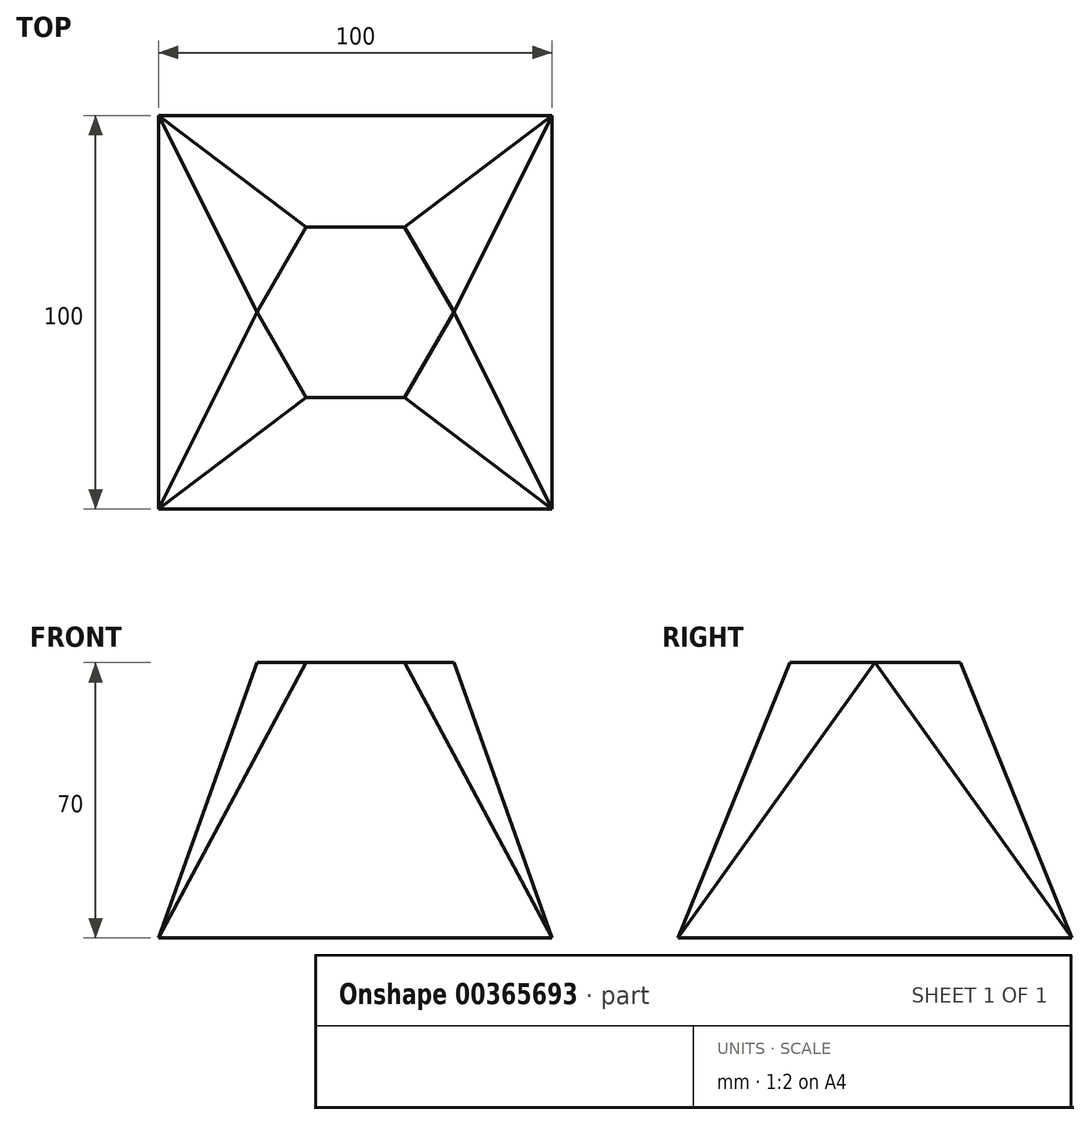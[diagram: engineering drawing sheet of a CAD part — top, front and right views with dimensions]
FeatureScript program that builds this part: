
annotation { "Feature Type Name" : "Feature", "Feature Type Description" : "" }
export const myFeature = defineFeature(function(context is Context, id is Id, definition is map)
    precondition{}
    {
        {
            var Q0;
            Q0=qCreatedBy(makeId("Top.planeOp"),FACE);
            cPlane(context, id + "F0", {"entities" : qUnion([Q0]), "cplaneType" : CPlaneType.OFFSET, "offset" : 70 * mm, "width" : 150 * mm, "height" : 150 * mm});
        }
        {
            var Q0;
            Q0=qCreatedBy(id+"F0.planeOp",FACE);
            var sketch = newSketch(context, id + "F1", { "sketchPlane" : qUnion([Q0])});
            skCircle(sketch, "E0.cCircle", {"center": v(0, 0) * mm, "radius": 25 * mm, "construction": true});
            skLineSegment(sketch, "E0.0", {"start": v(25, 0) * mm, "end": v(12.5, -21.65) * mm});
            skLineSegment(sketch, "E0.1", {"start": v(12.5, -21.65) * mm, "end": v(-12.5, -21.65) * mm});
            skLineSegment(sketch, "E0.2", {"start": v(-12.5, -21.65) * mm, "end": v(-25, 0) * mm});
            skLineSegment(sketch, "E0.3", {"start": v(-25, 0) * mm, "end": v(-12.5, 21.65) * mm});
            skLineSegment(sketch, "E0.4", {"start": v(-12.5, 21.65) * mm, "end": v(12.5, 21.65) * mm});
            skLineSegment(sketch, "E0.5", {"start": v(12.5, 21.65) * mm, "end": v(25, 0) * mm});
            skLineSegment(sketch, "E1", {"start": v(-12.5, 21.65) * mm, "end": v(-12.5, -21.65) * mm});
            skLineSegment(sketch, "E2", {"start": v(12.5, 21.65) * mm, "end": v(12.5, -21.65) * mm});
            skSolve(sketch);
        }
        {
            var Q0;
            Q0=qCreatedBy(makeId("Top.planeOp"),FACE);
            var sketch = newSketch(context, id + "F2", { "sketchPlane" : qUnion([Q0])});
            skLineSegment(sketch, "E3.bottom", {"start": v(50, -50) * mm, "end": v(-50, -50) * mm});
            skLineSegment(sketch, "E3.top", {"start": v(50, 50) * mm, "end": v(-50, 50) * mm});
            skLineSegment(sketch, "E3.left", {"start": v(50, -50) * mm, "end": v(50, 50) * mm});
            skLineSegment(sketch, "E3.right", {"start": v(-50, -50) * mm, "end": v(-50, 50) * mm});
            skPoint(sketch, "E3.middle", {"position": v(0, 0) * mm});
            skSolve(sketch);
        }
        {
            var Q0;
            Q0=makeQuery(id+"F1.imprint","IMPRINT",FACE,{"disambiguationData":[TD([[makeQuery(id+"F1.imprint","IMPRINT",EDGE,{"derivedFrom":sQuery(id+"F1.wireOp",EDGE,"E0.1")}),-1.0]])]});
            var Q1;
            Q1=makeQuery(id+"F2.imprint","IMPRINT",FACE,{"disambiguationData":[TD([[makeQuery(id+"F2.imprint","IMPRINT",EDGE,{"derivedFrom":sQuery(id+"F2.wireOp",EDGE,"E3.bottom")}),-1.0]])]});
            loft(context, id + "F3", {"sheetProfilesArray" : [{ "sheetProfileEntities" : qUnion([Q0]) }, { "sheetProfileEntities" : qUnion([Q1]) }]});
        }
        {
            var Q1;
            Q1=makeQuery(id+"F3.opLoft","MID_CAP_VERTEX",VERTEX,{"disambiguationData":[OSD([sQuery(id+"F2.wireOp",EDGE,"E3.bottom"),sQuery(id+"F2.wireOp",EDGE,"E3.left")])],"capPos":1.0});
            var Q2;
            Q2=makeQuery(id+"F1.imprint","IMPRINT",FACE,{"disambiguationData":[TD([[makeQuery(id+"F1.imprint","IMPRINT",EDGE,{"derivedFrom":sQuery(id+"F1.wireOp",EDGE,"E0.0")}),-1.0]])]});
            loft(context, id + "F4", {"operationType" : NewBodyOperationType.ADD, "sheetProfilesArray" : [{ "sheetProfileEntities" : qUnion([Q1]) }, { "sheetProfileEntities" : qUnion([Q2]) }]});
        }
        {
            var Q1;
            Q1=makeQuery(id+"F1.imprint","IMPRINT",FACE,{"disambiguationData":[TD([[makeQuery(id+"F1.imprint","IMPRINT",EDGE,{"derivedFrom":sQuery(id+"F1.wireOp",EDGE,"E0.0")}),-1.0]])]});
            var Q2;
            Q2=makeQuery(id+"F3.opLoft","MID_CAP_VERTEX",VERTEX,{"disambiguationData":[OSD([sQuery(id+"F2.wireOp",EDGE,"E3.top"),sQuery(id+"F2.wireOp",EDGE,"E3.left")])],"capPos":1.0});
            loft(context, id + "F5", {"operationType" : NewBodyOperationType.ADD, "sheetProfilesArray" : [{ "sheetProfileEntities" : qUnion([Q1]) }, { "sheetProfileEntities" : qUnion([Q2]) }]});
        }
        {
            var Q1;
            Q1=makeQuery(id+"F5.opLoft","SWEPT_FACE",FACE,{"disambiguationData":[OSD([sQuery(id+"F1.wireOp",EDGE,"E0.0"),sQuery(id+"F1.wireOp",EDGE,"E0.1"),sQuery(id+"F1.wireOp",EDGE,"E0.5"),sQuery(id+"F1.wireOp",EDGE,"E2")])]});
            var Q2;
            Q2=makeQuery(id+"F4.opLoft","SWEPT_FACE",FACE,{"disambiguationData":[OSD([sQuery(id+"F1.wireOp",EDGE,"E0.0"),sQuery(id+"F1.wireOp",EDGE,"E0.4"),sQuery(id+"F1.wireOp",EDGE,"E0.5"),sQuery(id+"F1.wireOp",EDGE,"E2")])]});
            var Q3;
            Q3=makeQuery(id+"F3.opLoft","MID_CAP_EDGE",EDGE,{"disambiguationData":[OSD([sQuery(id+"F2.wireOp",EDGE,"E3.bottom"),sQuery(id+"F2.wireOp",EDGE,"E3.top"),sQuery(id+"F2.wireOp",EDGE,"E3.left")])],"capPos":1.0});
            loft(context, id + "F6", {"operationType" : NewBodyOperationType.ADD, "addGuides" : true, "sheetProfilesArray" : [{ "sheetProfileEntities" : qUnion([Q1]) }, { "sheetProfileEntities" : qUnion([Q2]) }], "guidesArray" : [{ "guideEntities" : qUnion([Q3]), "guideDerivativeType" : LoftGuideDerivativeType.DEFAULT, "guideDerivativeMagnitude" : 1 }]});
        }
        {
            var Q1;
            Q1=makeQuery(id+"F1.imprint","IMPRINT",FACE,{"disambiguationData":[TD([[makeQuery(id+"F1.imprint","IMPRINT",EDGE,{"derivedFrom":sQuery(id+"F1.wireOp",EDGE,"E0.2")}),-1.0]])]});
            var Q2;
            Q2=makeQuery(id+"F3.opLoft","MID_CAP_VERTEX",VERTEX,{"disambiguationData":[OSD([sQuery(id+"F2.wireOp",EDGE,"E3.top"),sQuery(id+"F2.wireOp",EDGE,"E3.right")])],"capPos":1.0});
            loft(context, id + "F7", {"operationType" : NewBodyOperationType.ADD, "sheetProfilesArray" : [{ "sheetProfileEntities" : qUnion([Q1]) }, { "sheetProfileEntities" : qUnion([Q2]) }]});
        }
        {
            var Q1;
            Q1=makeQuery(id+"F1.imprint","IMPRINT",FACE,{"disambiguationData":[TD([[makeQuery(id+"F1.imprint","IMPRINT",EDGE,{"derivedFrom":sQuery(id+"F1.wireOp",EDGE,"E0.2")}),-1.0]])]});
            var Q2;
            Q2=makeQuery(id+"F3.opLoft","MID_CAP_VERTEX",VERTEX,{"disambiguationData":[OSD([sQuery(id+"F2.wireOp",EDGE,"E3.bottom"),sQuery(id+"F2.wireOp",EDGE,"E3.right")])],"capPos":1.0});
            loft(context, id + "F8", {"operationType" : NewBodyOperationType.ADD, "sheetProfilesArray" : [{ "sheetProfileEntities" : qUnion([Q1]) }, { "sheetProfileEntities" : qUnion([Q2]) }]});
        }
        {
            var Q1;
            Q1=makeQuery(id+"F7.opLoft","SWEPT_FACE",FACE,{"disambiguationData":[OSD([sQuery(id+"F1.wireOp",EDGE,"E0.1"),sQuery(id+"F1.wireOp",EDGE,"E0.2"),sQuery(id+"F1.wireOp",EDGE,"E0.3"),sQuery(id+"F1.wireOp",EDGE,"E1")])]});
            var Q2;
            Q2=makeQuery(id+"F8.opLoft","SWEPT_FACE",FACE,{"disambiguationData":[OSD([sQuery(id+"F1.wireOp",EDGE,"E0.2"),sQuery(id+"F1.wireOp",EDGE,"E0.3"),sQuery(id+"F1.wireOp",EDGE,"E0.4"),sQuery(id+"F1.wireOp",EDGE,"E1")])]});
            var Q3;
            Q3=makeQuery(id+"F3.opLoft","MID_CAP_EDGE",EDGE,{"disambiguationData":[OSD([sQuery(id+"F2.wireOp",EDGE,"E3.bottom"),sQuery(id+"F2.wireOp",EDGE,"E3.top"),sQuery(id+"F2.wireOp",EDGE,"E3.right")])],"capPos":1.0});
            loft(context, id + "F9", {"operationType" : NewBodyOperationType.ADD, "addGuides" : true, "sheetProfilesArray" : [{ "sheetProfileEntities" : qUnion([Q1]) }, { "sheetProfileEntities" : qUnion([Q2]) }], "guidesArray" : [{ "guideEntities" : qUnion([Q3]), "guideDerivativeType" : LoftGuideDerivativeType.DEFAULT, "guideDerivativeMagnitude" : 1 }]});
        }
    });
